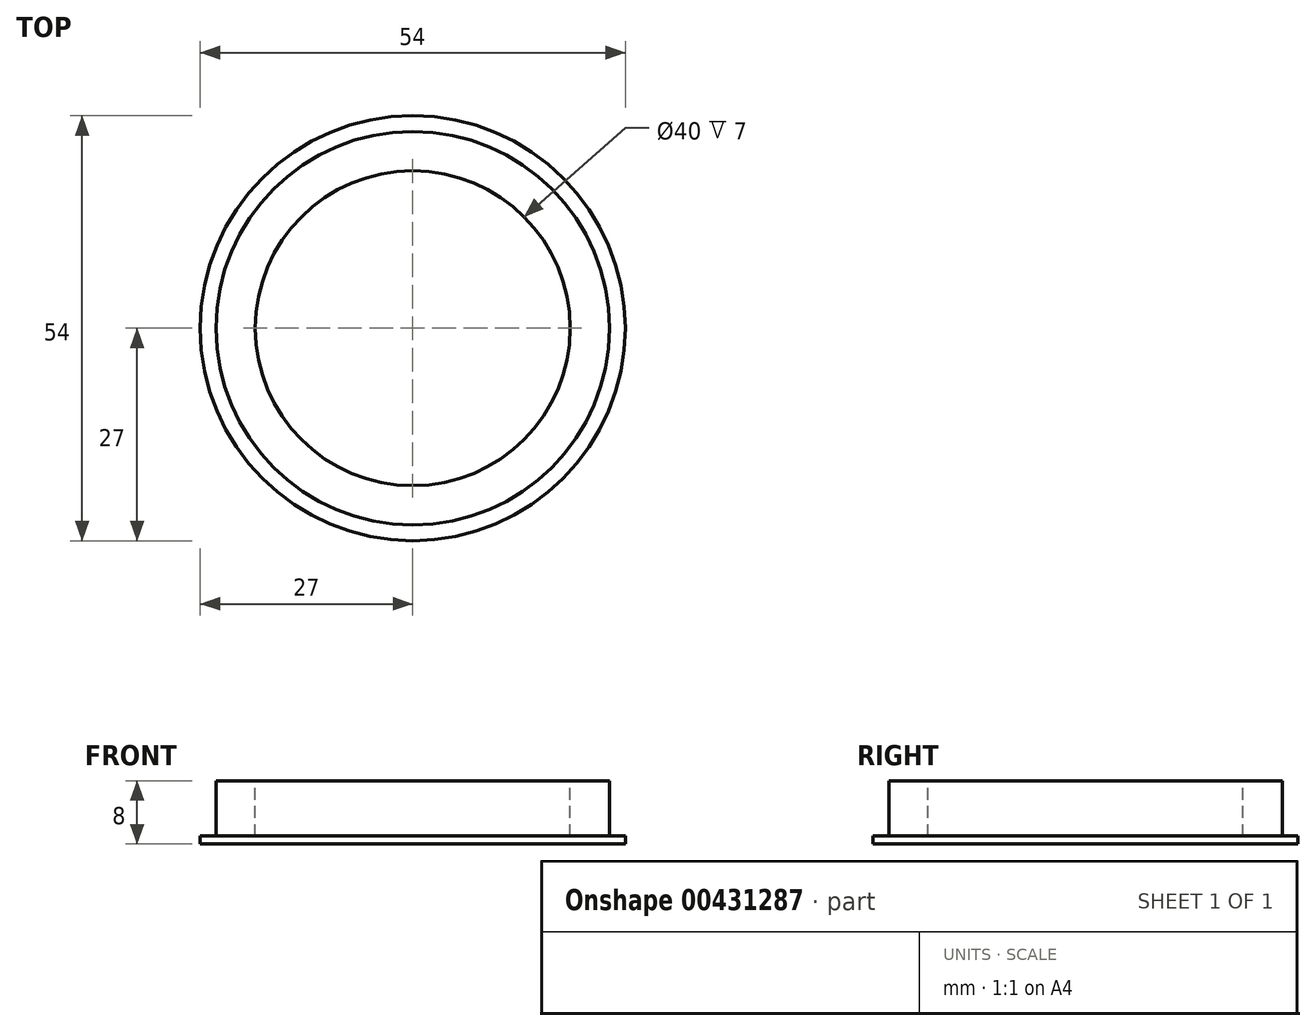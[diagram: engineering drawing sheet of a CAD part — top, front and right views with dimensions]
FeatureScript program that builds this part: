
annotation { "Feature Type Name" : "Feature", "Feature Type Description" : "" }
export const myFeature = defineFeature(function(context is Context, id is Id, definition is map)
    precondition{}
    {
        {
            var Q0;
            Q0=qCreatedBy(makeId("Top.planeOp"),FACE);
            var sketch = newSketch(context, id + "F0", { "sketchPlane" : qUnion([Q0])});
            skCircle(sketch, "E0", {"center": v(0, 0) * mm, "radius": 25 * mm});
            skCircle(sketch, "E1", {"center": v(0, 0) * mm, "radius": 27 * mm});
            skSolve(sketch);
        }
        {
            var Q0;
            Q0 = qSketchRegion(id + "F0", true);
            var Q1;
            Q1=makeQuery(id+"F0.imprint","IMPRINT",FACE,{"disambiguationData":[TD([[makeQuery(id+"F0.imprint","IMPRINT",EDGE,{"derivedFrom":sQuery(id+"F0.wireOp",EDGE,"E0")}),1.0]])]});
            extrude(context, id + "F1", {"entities" : qUnion([Q0, Q1]), "depth" : 1 * mm});
        }
        {
            var Q0;
            Q0=makeQuery(id+"F0.imprint","IMPRINT",FACE,{"disambiguationData":[TD([[makeQuery(id+"F0.imprint","IMPRINT",EDGE,{"derivedFrom":sQuery(id+"F0.wireOp",EDGE,"E0")}),1.0]])]});
            extrude(context, id + "F2", {"entities" : qUnion([Q0]), "operationType" : NewBodyOperationType.ADD, "depth" : 8 * mm});
        }
        {
            var Q0;
            Q0=makeQuery(id+"F2.opExtrude","CAP_FACE",FACE,{"disambiguationData":[OSD([sQuery(id+"F0.wireOp",EDGE,"E0")])],"isStart":false});
            var sketch = newSketch(context, id + "F3", { "sketchPlane" : qUnion([Q0])});
            skPoint(sketch, "E2.0", {"position": v(0, 0) * mm});
            skCircle(sketch, "E3", {"center": v(0, 0) * mm, "radius": 20 * mm});
            skSolve(sketch);
        }
        {
            var Q0;
            Q0=makeQuery(id+"F3.imprint","IMPRINT",FACE,{"disambiguationData":[TD([[makeQuery(id+"F3.imprint","IMPRINT",EDGE,{"derivedFrom":sQuery(id+"F3.wireOp",EDGE,"E3")}),1.0]])]});
            extrude(context, id + "F4", {"entities" : qUnion([Q0]), "operationType" : NewBodyOperationType.REMOVE, "oppositeDirection" : true, "depth" : 7 * mm});
        }
    });
